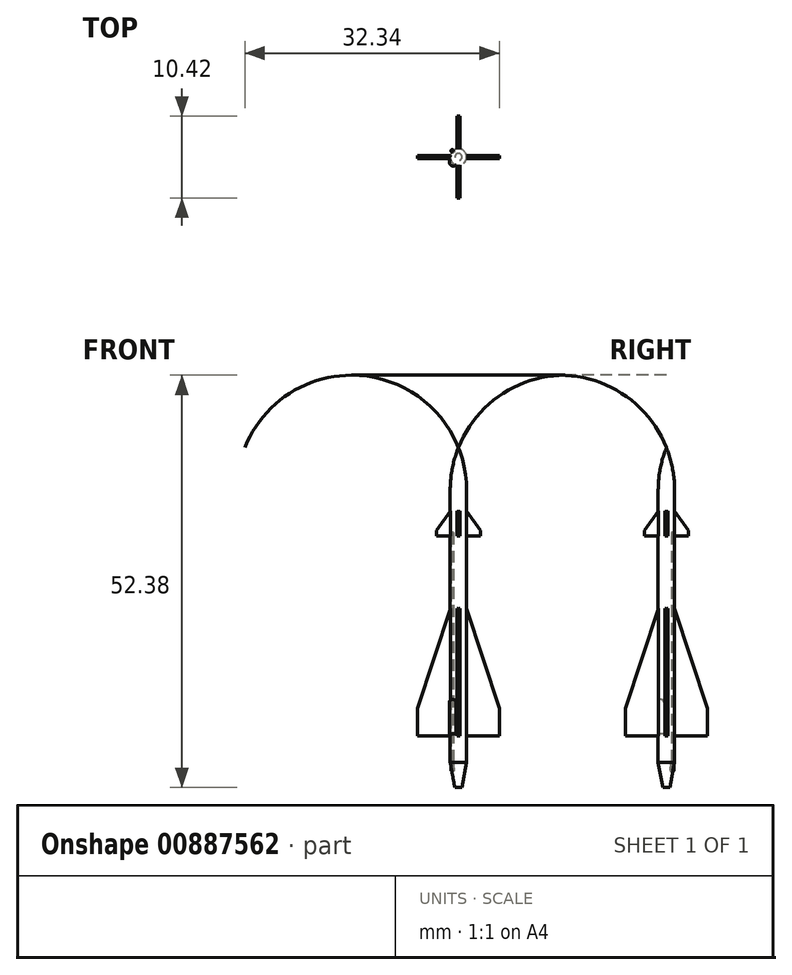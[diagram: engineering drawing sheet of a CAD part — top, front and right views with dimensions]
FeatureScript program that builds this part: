
annotation { "Feature Type Name" : "Feature", "Feature Type Description" : "" }
export const myFeature = defineFeature(function(context is Context, id is Id, definition is map)
    precondition{}
    {
        {
            var Q0;
            Q0=qCreatedBy(makeId("Front.planeOp"),FACE);
            var sketch = newSketch(context, id + "F0", { "sketchPlane" : qUnion([Q0])});
            skLineSegment(sketch, "E0", {"start": v(0, 0) * mm, "end": v(0, 43.2) * mm});
            skLineSegment(sketch, "E1", {"start": v(1.04, 37.78) * mm, "end": v(1.04, 0) * mm});
            skLineSegment(sketch, "E2", {"start": v(1.04, 0) * mm, "end": v(0, 0) * mm});
            skArc(sketch, "E3", {"start": v(1.04, 37.78) * mm, "mid": v(0.78, 40.54) * mm, "end": v(0, 43.2) * mm});
            skLineSegment(sketch, "E4", {"start": v(0.45, 0) * mm, "end": v(1.04, 3.2) * mm});
            skSolve(sketch);
        }
        {
            var Q0;
            Q0=makeQuery(id+"F0.imprint","IMPRINT",FACE,{"disambiguationData":[TD([[makeQuery(id+"F0.imprint","IMPRINT",EDGE,{"derivedFrom":sQuery(id+"F0.wireOp",EDGE,"E0")}),-1.0]])]});
            var Q1;
            Q1=sQuery(id+"F0.wireOp",EDGE,"E0");
            revolve(context, id + "F1", {"surfaceOperationType" : NewSurfaceOperationType.NEW, "entities" : qUnion([Q0]), "axis" : qUnion([Q1]), "revolveType" : RevolveType.FULL});
        }
        {
            var Q0;
            Q0=qCreatedBy(makeId("Front.planeOp"),FACE);
            var sketch = newSketch(context, id + "F2", { "sketchPlane" : qUnion([Q0])});
            skLineSegment(sketch, "E5.0", {"start": v(1.04, 37.78) * mm, "end": v(-1.04, 37.78) * mm, "construction": true});
            skLineSegment(sketch, "E6", {"start": v(0, 6.53) * mm, "end": v(5.2, 6.53) * mm});
            skLineSegment(sketch, "E7", {"start": v(5.2, 6.53) * mm, "end": v(5.2, 10.07) * mm});
            skLineSegment(sketch, "E8", {"start": v(5.2, 10.07) * mm, "end": v(1.04, 22.7) * mm});
            skLineSegment(sketch, "E9", {"start": v(0.4, 24.65) * mm, "end": v(0.4, 31.94) * mm});
            skLineSegment(sketch, "E10", {"start": v(0.4, 31.94) * mm, "end": v(2.78, 31.94) * mm});
            skLineSegment(sketch, "E11", {"start": v(2.78, 31.94) * mm, "end": v(2.78, 32.64) * mm});
            skLineSegment(sketch, "E12", {"start": v(2.78, 32.64) * mm, "end": v(0, 36.53) * mm});
            skLineSegment(sketch, "E13", {"start": v(0, 36.53) * mm, "end": v(0, 6.53) * mm});
            skLineSegment(sketch, "E14", {"start": v(1.04, 37.78) * mm, "end": v(1.04, 0) * mm, "construction": true});
            skPoint(sketch, "E15", {"position": v(1.04, 6.53) * mm});
            skPoint(sketch, "E16", {"position": v(1.04, 35.07) * mm});
            skLineSegment(sketch, "E17", {"start": v(1.04, 22.7) * mm, "end": v(0.4, 24.65) * mm});
            skLineSegment(sketch, "E18", {"start": v(1.04, 3.2) * mm, "end": v(0.45, 0) * mm});
            skSolve(sketch);
        }
        {
            var Q0;
            Q0=qSketchRegion(id+"F2",true);
            extrude(context, id + "F3", {"entities" : qUnion([Q0]), "operationType" : NewBodyOperationType.ADD, "oppositeDirection" : true, "depth" : .4 * mm, "offsetDistance" : 25 * mm, "symmetric" : true});
        }
        {
            var Q0;
            Q0=makeQuery(id+"F1.opRevolve","SWEPT_BODY",BODY,{"disambiguationData":[OSD([sQuery(id+"F0.wireOp",EDGE,"E0"),sQuery(id+"F0.wireOp",EDGE,"E1"),sQuery(id+"F0.wireOp",EDGE,"E2"),sQuery(id+"F0.wireOp",EDGE,"h1jDSi8t-veb7-85qg-XgDk-6E8DmZjBuz4r")])]});
            var Q1;
            Q1=makeQuery(id+"F1.opRevolve","SWEPT_FACE",FACE,{"disambiguationData":[OSD([sQuery(id+"F0.wireOp",EDGE,"E1")])]});
            circularPattern(context, id + "F4", {"operationType" : NewBodyOperationType.ADD, "entities" : qUnion([Q0]), "axis" : qUnion([Q1]), "angle" : 360 * degree, "instanceCount" : 4, "equalSpace" : true, "computeTransformsWithoutBuiltin" : true});
        }
        {
            var Q0;
            Q0=qCreatedBy(makeId("Top.planeOp"),FACE);
            cPlane(context, id + "F5", {"entities" : qUnion([Q0]), "cplaneType" : CPlaneType.OFFSET, "offset" : (980 / 144) * mm, "width" : 150 * mm, "height" : 150 * mm});
        }
        {
            var Q0;
            Q0=qCreatedBy(id+"F5.planeOp",FACE);
            var sketch = newSketch(context, id + "F6", { "sketchPlane" : qUnion([Q0])});
            skLineSegment(sketch, "E19", {"start": v(-1, -0.3) * mm, "end": v(-0.7, 0) * mm});
            skLineSegment(sketch, "E20", {"start": v(-0.7, 0) * mm, "end": v(0, -0.7) * mm});
            skLineSegment(sketch, "E21", {"start": v(0, -0.7) * mm, "end": v(-0.3, -1) * mm});
            skArc(sketch, "E22", {"start": v(-1, -0.3) * mm, "mid": v(-1, -1) * mm, "end": v(-0.3, -1) * mm});
            skLineSegment(sketch, "E23", {"start": v(-0.35, -0.35) * mm, "end": v(0, 0) * mm, "construction": true});
            skLineSegment(sketch, "E24", {"start": v(0, 0) * mm, "end": v(-2.42, 0) * mm, "construction": true});
            skCircle(sketch, "E25.0", {"center": v(0, 0) * mm, "radius": 1.04 * mm});
            skSolve(sketch);
        }
        {
            var Q0;
            Q0=qSketchRegion(id+"F6",true);
            extrude(context, id + "F7", {"entities" : qUnion([Q0]), "operationType" : NewBodyOperationType.ADD, "depth" : (630 / 144) * mm, "offsetDistance" : 25 * mm});
        }
        {
            var Q0;
            Q0=makeQuery(id+"F7.opExtrude","CAP_EDGE",EDGE,{"disambiguationData":[OSD([sQuery(id+"F6.wireOp",EDGE,"E22")])],"isStart":false});
            fillet(context, id + "F8", {"entities" : qUnion([Q0]), "radius" : .4 * mm, "tangentPropagation" : true, "allowEdgeOverflow" : false});
        }
        {
            var Q0;
            Q0=qCreatedBy(makeId("Top.planeOp"),FACE);
            cPlane(context, id + "F9", {"entities" : qUnion([Q0]), "cplaneType" : CPlaneType.OFFSET, "offset" : (300 / 144) * mm, "width" : 150 * mm, "height" : 150 * mm});
        }
        {
            var Q0;
            Q0=qCreatedBy(id+"F9.planeOp",FACE);
            var sketch = newSketch(context, id + "F10", { "sketchPlane" : qUnion([Q0])});
            skCircle(sketch, "E26.0", {"center": v(0, 0) * mm, "radius": 1.04 * mm});
            skLineSegment(sketch, "E27", {"start": v(-0.35, 0.14) * mm, "end": v(-0.14, 0.35) * mm});
            skLineSegment(sketch, "E28", {"start": v(-0.14, 0.35) * mm, "end": v(-0.7, 0.9) * mm});
            skLineSegment(sketch, "E29", {"start": v(-0.35, 0.14) * mm, "end": v(-0.9, 0.7) * mm});
            skLineSegment(sketch, "E30", {"start": v(0, 0) * mm, "end": v(-0.25, 0.25) * mm, "construction": true});
            skLineSegment(sketch, "E31", {"start": v(0, 0) * mm, "end": v(-0.55, 0) * mm, "construction": true});
            skArc(sketch, "E32", {"start": v(-0.7, 0.9) * mm, "mid": v(-0.9, 0.9) * mm, "end": v(-0.9, 0.7) * mm});
            skSolve(sketch);
        }
        {
            var Q0;
            {var subQ5=sQuery(id+"F10.wireOp",EDGE,"E27");Q0=makeQuery(id+"F10.imprint","IMPRINT",FACE,{"disambiguationData":[TD([[makeQuery(id+"F10.imprint","IMPRINT",EDGE,{"derivedFrom":subQ5}),1.0]])]});}
            var Q1;
            {var subQ5=sQuery(id+"F10.wireOp",EDGE,"E32");Q1=makeQuery(id+"F10.imprint","IMPRINT",FACE,{"disambiguationData":[TD([[makeQuery(id+"F10.imprint","IMPRINT",EDGE,{"derivedFrom":subQ5}),1.0]])]});}
            extrude(context, id + "F11", {"entities" : qUnion([Q0, Q1]), "operationType" : NewBodyOperationType.ADD, "depth" : (4300 / 144) * mm, "offsetDistance" : 25 * mm});
        }
        {
            var Q0;
            Q0=makeQuery(id+"F11.boolean.opBoolean","INTERSECT",EDGE,{"derivedFrom":[makeQuery(id+"F1.opRevolve","SWEPT_FACE",FACE,{"disambiguationData":[OSD([sQuery(id+"F0.wireOp",EDGE,"E1")])]}),makeQuery(id+"F11.opExtrude","CAP_FACE",FACE,{"disambiguationData":[OSD([sQuery(id+"F10.wireOp",EDGE,"E27"),sQuery(id+"F10.wireOp",EDGE,"E28"),sQuery(id+"F10.wireOp",EDGE,"E29"),sQuery(id+"F10.wireOp",EDGE,"E32")])],"isStart":false})]});
            chamfer(context, id + "F12", {"entities" : qUnion([Q0]), "chamferType" : ChamferType.OFFSET_ANGLE, "width" : .25 * mm, "oppositeDirection" : true, "angle" : 60 * degree, "tangentPropagation" : true});
        }
    });
